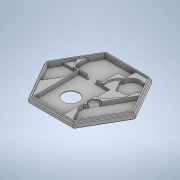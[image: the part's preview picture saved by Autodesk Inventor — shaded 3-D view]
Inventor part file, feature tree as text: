
AUTODESK INVENTOR PART (.ipt)
format: ipt  version: 2021 (Build 250183000, 183)  size: 616,960 bytes
history: native  units: mm
features: extrude x8, projected_geometry x6, sketch x5, other x2, plane x1, loft x1, fillet x1, chamfer x1
ambient origin geometry x8: Origin, YZ Plane, XZ Plane, XY Plane, X Axis, Y Axis, Z Axis, Center Point
bodies: Solid1 (feature_tree)
feature tree (25):
  extrude  "Extrusion1"  Depth=0.2mm
  extrude  "Extrusion2"  Depth=1.0mm TaperAngle=0.0deg
  extrude  "Extrusion3"  Depth=108.4mm
  extrude  "Extrusion4"  Depth=43.0mm
  extrude  "Extrusion5"  Depth=2.0mm
  extrude  "Extrusion6"  Depth=2.0mm
  extrude  "Extrusion8"  Depth=1.5mm
  extrude  "Extrusion9"  Depth=1.5mm
  plane  "Work Plane1"
  loft  "Loft1"
  fillet  "Fillet2"  Radius=4.5mm
  chamfer  "Chamfer1"  [1 undecoded]
  sketch  "Sketch2"  dims[d0=102.0mm d2=0.2mm]
  projected_geometry  "Projected Loop1"
  sketch  "Sketch3"  dims[d8=1.0mm d9=0.0mm d10=7.5mm d11=0.0mm]
  projected_geometry  "Projected Loop2"
  sketch  "Sketch5"  dims[d16=108.4mm d17=42.0mm]
  projected_geometry  "Projected Loop4"
  sketch  "Sketch7"  dims[d18=64.0mm d19=43.0mm]
  projected_geometry  "Projected Loop6"
  sketch  "Sketch9"  dims[d21=24.8mm d22=21.8mm d26=65.0mm d27=1.5mm d28=1.5mm d29=1.5mm d30=4.5mm d31=0.0mm d32=5.5mm d33=0.0mm d36=25.25mm d37=0.5mm d38=31.7mm d39=0.5mm d41=24.8mm d42=21.8mm d43=0.5mm d44=1.0mm d45=0.5mm d46=0.25mm d47=0.5mm d50=35.5mm d54=45.0deg d55=2.0mm d56=1.0mm d67=0.5mm d74=0.5mm d77=0.5mm d78=0.5mm d79=0.5mm d80=0.5mm d81=0.5mm d83=0.5mm d84=0.5mm d85=1.5mm d86=45.0deg d87=2.0mm d88=12.5mm d89=20.9mm d90=0.5mm d91=1.5mm d92=0.5mm d93=0.5mm d94=0.5mm d95=0.5mm d96=0.5mm d97=0.5mm d98=0.5mm d99=0.5mm d100=0.5mm d102=1.5mm d103=0.5mm d105=2.0mm d106=0.0mm d109=0.5mm d110=1.0mm d111=1.5mm d112=1.0mm d113=25.25mm d114=16.4mm d115=0.5mm d116=7.2mm d117=22.0mm d118=10.0mm d121=10.0mm d122=0.0mm d126=10.0mm d127=0.5mm d128=0.0mm d132=0.5mm d133=0.5mm d134=0.5mm d135=0.75mm d136=8.5mm d137=0.5mm d138=0.0mm d140=6.5mm d141=0.0mm d142=90.0deg d143=0.0mm d144=90.0deg d145=0.0mm d146=90.0deg d147=0.5mm d148=1.0mm d149=2.0mm d150=45.0deg d151=2.0mm]
  projected_geometry  "Projected Loop8"
  projected_geometry  "Projected Loop9"
  other  "Edges1"
  other  "Edges2"
note: 1 required parameter value undecoded (feature->parameter linkage not recoverable at this tier; creation-order binding heuristic only, values carry confidence <= 0.55)
